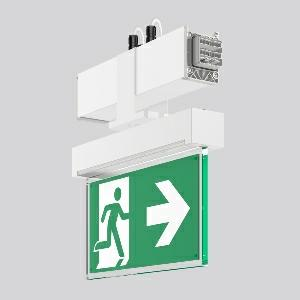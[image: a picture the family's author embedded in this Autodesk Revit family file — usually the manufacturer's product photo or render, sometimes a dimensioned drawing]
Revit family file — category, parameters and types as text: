
# Revit family: linedo_module_rz_9503rz_762_437_030_fe08
name_source: partatom
category: Lighting Fixtures
units: mm (PartAtom-declared; Revit-internal decimal feet)

## family parameters
Cut with Voids When Loaded = No
Host = Face
Light Source = No
Part Type = Normal
Room Calculation Point = No
Round Connector Dimension = Use Diameter
Shared = No

## types (1)
- LINEDO Module RZ
    Apparent Load = 0 VA
    Default Elevation = 1800 mm
    Description = LINEDO, white, on/off
Continuous line luminaire, L 336 B 62 H 343, SBS, 3 h, DALI-Sibe
    Height = 343 mm
    Lamp = 0 x
    Length = 336 mm
    Luminous efficacy = 0 lm/W
    Manufacturer = RZB
    ModVariant = No
    Model = 9503RZ.762.437.030
    Mounting Place = Ceiling
    Mounting Type = Surface mounted
    Number of Poles = 1
    OnlyDefault = Yes
    Power Factor = 1
    Product Name = LINEDO Module RZ
    Product group = Continuous line luminaire system Linedo IP 54
    ProductGroupID = 314
    Protection Class = Protection class I
    Protection Degree = IP 54
    RLX_Detail_Level = 1
    RLX_Emergency_Light_Flux = 0 lm
    RLX_Emergency_Type = 0
    RLX_Emergency_Type_DB = No
    RlxData = <blob elided: 35717 chars, md5=813b22f3>
    Standby Power = 0 W
    System Light Flux = 0 lm
    System Power = 0 W
    Type Comments = Product without accessories
    Type Image = 9503rz.762.434.030.jpg
    URL = http://relux.com
    VarID = ---
    Voltage = 0 V
    Weight = 0.00 kg
    Width = 62 mm  [stored 0.203412 ft]

note: [stored X ft] marks values corroborated as IEEE doubles in the binary element streams (Revit-internal decimal feet)

## geometry (parser evidence)
native form markers: Blend x4, Sweep x10
no freeform markers — native parametric forms only
